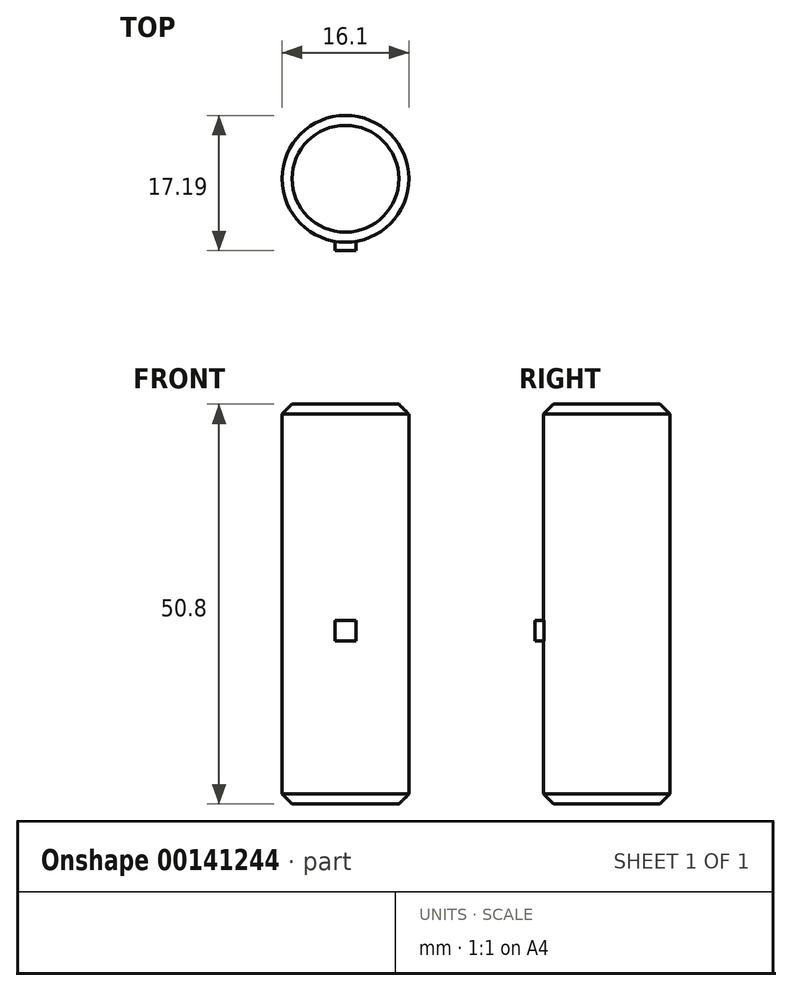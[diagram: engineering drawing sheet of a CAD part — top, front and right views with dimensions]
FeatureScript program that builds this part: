
annotation { "Feature Type Name" : "Feature", "Feature Type Description" : "" }
export const myFeature = defineFeature(function(context is Context, id is Id, definition is map)
    precondition{}
    {
        {
            var Q0;
            Q0=qCreatedBy(makeId("Top.planeOp"),FACE);
            var sketch = newSketch(context, id + "F0", { "sketchPlane" : qUnion([Q0])});
            skCircle(sketch, "E0", {"center": v(0, 0) * mm, "radius": 8.05 * mm});
            skSolve(sketch);
        }
        {
            var Q0;
            Q0=makeQuery(id+"F0.imprint","IMPRINT",FACE,{"disambiguationData":[TD([[makeQuery(id+"F0.imprint","IMPRINT",EDGE,{"derivedFrom":sQuery(id+"F0.wireOp",EDGE,"E0")}),1.0]])]});
            extrude(context, id + "F1", {"entities" : qUnion([Q0]), "depth" : 50.8 * mm});
        }
        {
            var Q0;
            Q0=makeQuery(id+"F1.opExtrude","CAP_EDGE",EDGE,{"disambiguationData":[OSD([sQuery(id+"F0.wireOp",EDGE,"E0")])],"isStart":false});
            chamfer(context, id + "F2", {"entities" : qUnion([Q0]), "width" : 1.27 * mm});
        }
        {
            var Q0;
            Q0=makeQuery(id+"F1.opExtrude","CAP_EDGE",EDGE,{"disambiguationData":[OSD([sQuery(id+"F0.wireOp",EDGE,"E0")])],"isStart":true});
            chamfer(context, id + "F3", {"entities" : qUnion([Q0]), "width" : 1.27 * mm});
        }
        {
            var Q0;
            Q0=qCreatedBy(makeId("Front.planeOp"),FACE);
            var sketch = newSketch(context, id + "F4", { "sketchPlane" : qUnion([Q0])});
            skLineSegment(sketch, "E1.bottom", {"start": v(1.34, 23.31) * mm, "end": v(-1.34, 23.31) * mm});
            skLineSegment(sketch, "E1.top", {"start": v(1.34, 20.75) * mm, "end": v(-1.34, 20.75) * mm});
            skLineSegment(sketch, "E1.left", {"start": v(1.34, 23.31) * mm, "end": v(1.34, 20.75) * mm});
            skLineSegment(sketch, "E1.right", {"start": v(-1.34, 23.31) * mm, "end": v(-1.34, 20.75) * mm});
            skPoint(sketch, "E1.middle", {"position": v(0, 22.03) * mm});
            skSolve(sketch);
        }
        {
            var Q0;
            Q0 = qSketchRegion(id + "F4", true);
            extrude(context, id + "F5", {"entities" : qUnion([Q0]), "operationType" : NewBodyOperationType.ADD, "depth" : 9.14 * mm});
        }
    });
